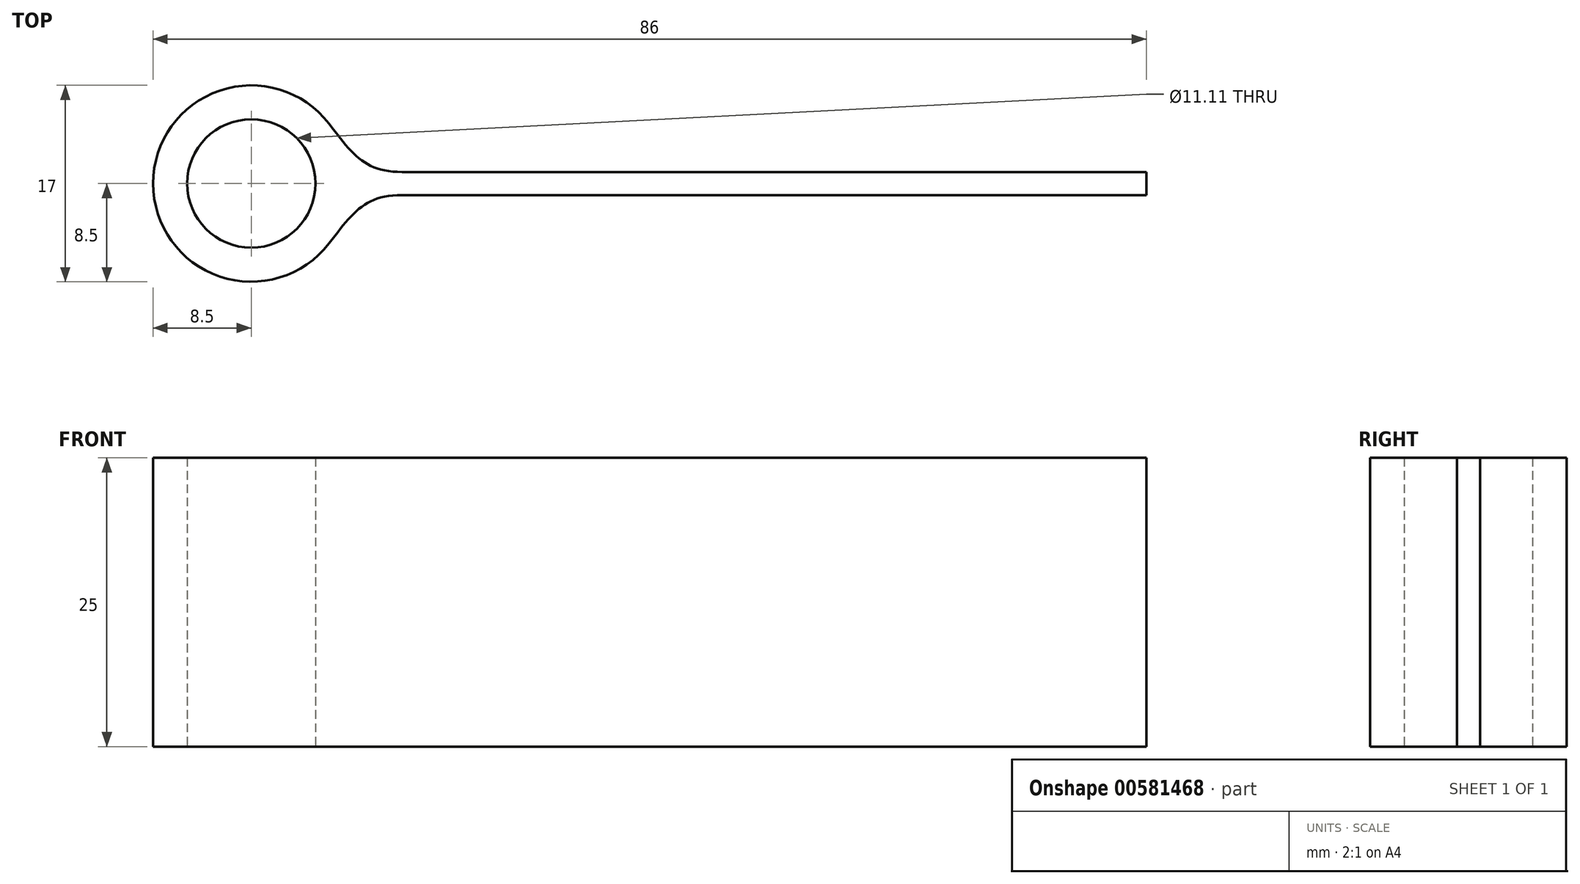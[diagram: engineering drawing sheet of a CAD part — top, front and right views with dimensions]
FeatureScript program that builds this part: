
annotation { "Feature Type Name" : "Feature", "Feature Type Description" : "" }
export const myFeature = defineFeature(function(context is Context, id is Id, definition is map)
    precondition{}
    {
        {
            var Q0;
            Q0=qCreatedBy(makeId("Top.planeOp"),FACE);
            var sketch = newSketch(context, id + "F0", { "sketchPlane" : qUnion([Q0])});
            skCircle(sketch, "E0", {"center": v(-77.5, 0) * mm, "radius": 5.56 * mm});
            skCircle(sketch, "E1", {"center": v(-77.5, 0) * mm, "radius": 8.5 * mm});
            skLineSegment(sketch, "E2", {"start": v(0, 0) * mm, "end": v(-77.5, 0) * mm, "construction": true});
            skLineSegment(sketch, "E3", {"start": v(-69.06, 1) * mm, "end": v(0, 1) * mm});
            skLineSegment(sketch, "E4.MirrorCS", {"start": v(-69.06, -1) * mm, "end": v(0, -1) * mm});
            skFitSpline(sketch, "E5", {"points": [v(-64.44, 1) * mm, v(-70.76, 5.18) * mm], "startDerivative": vector(-9.82, 0) * mm, "endDerivative": vector(-6.1, 7.92) * mm});
            skLineSegment(sketch, "E6", {"start": v(-73.31, 8.5) * mm, "end": v(-68.21, 1.87) * mm, "construction": true});
            skFitSpline(sketch, "E7.MirrorCS", {"points": [v(-64.44, -1) * mm, v(-70.76, -5.18) * mm], "startDerivative": vector(-9.82, 0) * mm, "endDerivative": vector(-6.1, -7.92) * mm});
            skLineSegment(sketch, "E8", {"start": v(0, 1) * mm, "end": v(0, -1) * mm});
            skSolve(sketch);
        }
        {
            var Q0;
            Q0=makeQuery(id+"F0.imprint","IMPRINT",FACE,{"disambiguationData":[TD([[makeQuery(id+"F0.imprint","IMPRINT",EDGE,{"derivedFrom":sQuery(id+"F0.wireOp",EDGE,"E0")}),-1.0]])]});
            var Q1;
            {var subQ3=sQuery(id+"F0.wireOp",EDGE,"E5");Q1=makeQuery(id+"F0.imprint","IMPRINT",FACE,{"disambiguationData":[TD([[makeQuery(id+"F0.imprint","IMPRINT",EDGE,{"derivedFrom":subQ3}),1.0]])]});}
            var Q2;
            {var subQ4=sQuery(id+"F0.wireOp",EDGE,"gpCLNrVA-YOMl-uCmA-3seF-2ul9ohdP6RrM");Q2=makeQuery(id+"F0.imprint","IMPRINT",FACE,{"disambiguationData":[TD([[makeQuery(id+"F0.imprint","IMPRINT",EDGE,{"derivedFrom":subQ4}),-1.0]])]});}
            var Q3;
            {var subQ3=sQuery(id+"F0.wireOp",EDGE,"E7.MirrorCS");Q3=makeQuery(id+"F0.imprint","IMPRINT",FACE,{"disambiguationData":[TD([[makeQuery(id+"F0.imprint","IMPRINT",EDGE,{"derivedFrom":subQ3}),-1.0]])]});}
            var Q4;
            {var subQ1=sQuery(id+"F0.wireOp",EDGE,"E1");var subQ11=sQuery(id+"F0.wireOp",EDGE,"E3");var subQ14=makeQuery(id+"F0.imprint","INTERSECT",VERTEX,{"derivedFrom":[subQ1,subQ11]});Q4=makeQuery(id+"F0.imprint","IMPRINT",FACE,{"disambiguationData":[TD([[makeQuery(id+"F0.imprint","IMPRINT",EDGE,{"disambiguationData":[TD([[subQ14,1.0]])],"derivedFrom":subQ1}),-1.0]])]});}
            var Q5;
            {var subQ3=sQuery(id+"F0.wireOp",EDGE,"E4.MirrorCS");var subQ11=sQuery(id+"F0.wireOp",EDGE,"gpCLNrVA-YOMl-uCmA-3seF-2ul9ohdP6RrM");var subQ12=makeQuery(id+"F0.imprint","INTERSECT",VERTEX,{"derivedFrom":[subQ3,subQ11]});Q5=makeQuery(id+"F0.imprint","IMPRINT",FACE,{"disambiguationData":[TD([[makeQuery(id+"F0.imprint","IMPRINT",EDGE,{"disambiguationData":[TD([[subQ12,1.0]])],"derivedFrom":subQ3}),-1.0]])]});}
            var Q6;
            {var subQ5=sQuery(id+"F0.wireOp",EDGE,"gpCLNrVA-YOMl-uCmA-3seF-2ul9ohdP6RrM");var subQ7=sQuery(id+"F0.wireOp",EDGE,"E3");var subQ8=makeQuery(id+"F0.imprint","INTERSECT",VERTEX,{"derivedFrom":[subQ7,subQ5]});Q6=makeQuery(id+"F0.imprint","IMPRINT",FACE,{"disambiguationData":[TD([[makeQuery(id+"F0.imprint","IMPRINT",EDGE,{"disambiguationData":[TD([[subQ8,1.0]])],"derivedFrom":subQ7}),1.0]])]});}
            var Q7;
            Q7=makeQuery(id+"F0.imprint","IMPRINT",FACE,{"disambiguationData":[TD([[makeQuery(id+"F0.imprint","IMPRINT",EDGE,{"derivedFrom":sQuery(id+"F0.wireOp",EDGE,"cdb4b34e-ad33-432d-9698-47c2aafa087e.2.0")}),-1.0]])]});
            extrude(context, id + "F1", {"entities" : qUnion([Q0, Q1, Q2, Q3, Q4, Q5, Q6, Q7]), "depth" : 25 * mm, "offsetDistance" : 25 * mm});
        }
    });
